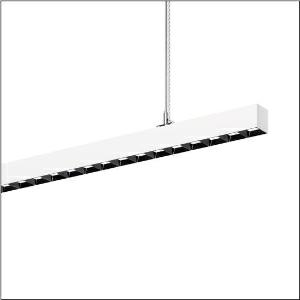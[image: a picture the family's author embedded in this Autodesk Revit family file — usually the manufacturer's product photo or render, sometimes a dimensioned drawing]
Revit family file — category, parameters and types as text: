
# Revit family: silica_21_51mx34dc4dwb
name_source: partatom
category: Lighting Fixtures
units: mm (PartAtom-declared; Revit-internal decimal feet)

## family parameters
Cut with Voids When Loaded = No
Host = Face
Light Source = No
Part Type = Normal
Room Calculation Point = No
Round Connector Dimension = Use Diameter
Shared = No

## types (1)
- --- (1 x LED, 19200 lm, 120.3 W, 4000K)
    Apparent Load = 120 VA
    CIE Flux Codes = 74 94 99 56 100
    Color Rendering = 80
    Color Temperature = 4000K
    Default Elevation = 1800 mm
    Description = Silica 21, office luminaire, primary light control with darklight reflector, of PMMA, black, light emission: direct/indirect distribution, primary light characteristic: asymmetric, installation type: suspended mounting, LED, rated luminous flux: 19.200lm, luminous efficacy: 160lm/W, light colour: 840, colour temperature: 4000K, control gear: DALI 2, with terminal, 3+2-pole, max. 2.5mm², mains connection: 220..240V, AC, 50/60Hz, rated input power: 120.3W, luminaire housing, of aluminium, traffic white (RAL 9016), length: 3.004mm, width: 53mm, height: 53mm, protection rating (complete): IP20, insulation class (complete): insulation class I (protective earthing), certification: CE, permissible operating ambient temperature: 0..+35°C, standard: EN 50419, packaging unit: 1 piece
    Height = 53 mm
    Lamp = 1 x LED
    Lamp Light Flux = 19200 lm
    Lamp Power = 120.3 W
    Lamp count = 1
    Length = 3004 mm
    Luminous efficacy = 160 lm/W
    Manufacturer = Siteco
    ModVariant = No
    Model = 51MX34DC4DWB
    Mounting Place = Ceiling
    Mounting Type = Pendant
    Number of Poles = 1
    OnlyDefault = Yes
    Power Factor = 1
    Product Name = Silica 21
    Product group = office luminaire | ceiling pendant
    ProductGroupID = 903
    Protection Class = Protection class I
    Protection Degree = IP 20
    RLX_Detail_Level = 1
    RLX_Emergency_Light_Flux = 0 lm
    RLX_Emergency_Type = 0
    RLX_Emergency_Type_DB = No
    RlxData = <blob elided: 65253 chars, md5=ad275fdc>
    Socket = socket
    Standby Power = 0 W
    System Light Flux = 19200 lm
    System Power = 120 W
    Type Comments = factory setting: luminous flux: 100 % | dim-lin: 254 | 418 mA
    Type Image = l_1335871.jpg
    URL = http://relux.com
    VarID = @adj_122027
    Voltage = 0 V
    Weight = 0.00 kg
    Width = 53 mm

## geometry (parser evidence)
native form markers: Blend x4, Sweep x11
no freeform markers — native parametric forms only
